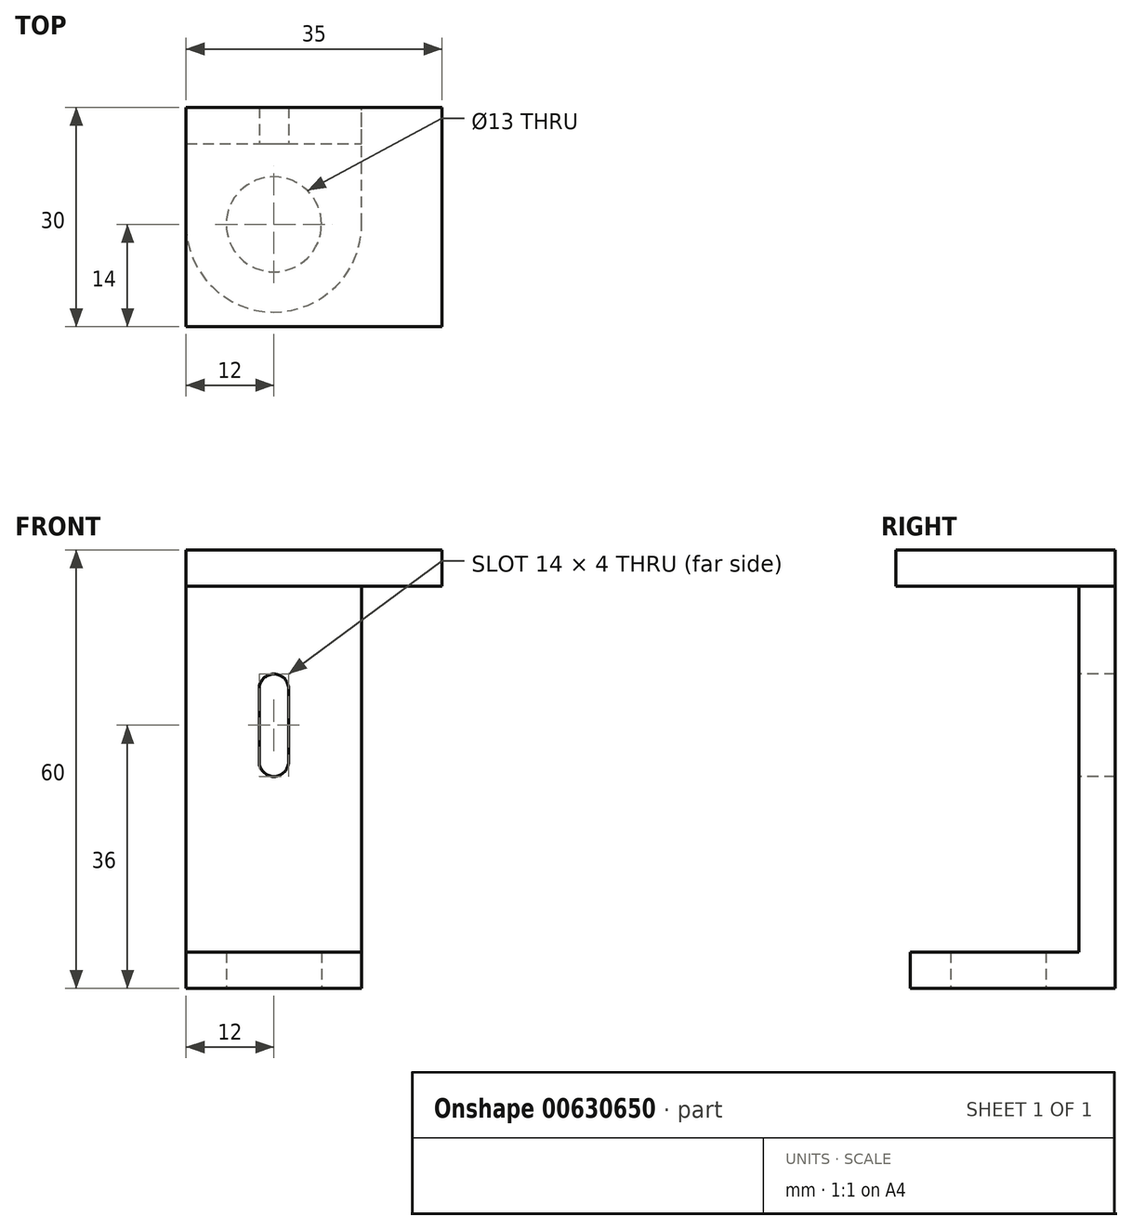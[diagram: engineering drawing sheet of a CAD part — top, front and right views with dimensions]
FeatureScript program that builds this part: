
annotation { "Feature Type Name" : "Feature", "Feature Type Description" : "" }
export const myFeature = defineFeature(function(context is Context, id is Id, definition is map)
    precondition{}
    {
        {
            var Q0;
            Q0=qCreatedBy(makeId("Top.planeOp"),FACE);
            var sketch = newSketch(context, id + "F0", { "sketchPlane" : qUnion([Q0])});
            skCircle(sketch, "E0", {"center": v(0, 0) * mm, "radius": 6.5 * mm});
            skArc(sketch, "E1", {"start": v(-12, 0) * mm, "mid": v(0, -12) * mm, "end": v(12, 0) * mm});
            skLineSegment(sketch, "E2.top", {"start": v(-12, 16) * mm, "end": v(12, 16) * mm});
            skLineSegment(sketch, "E2.left", {"start": v(-12, 0) * mm, "end": v(-12, 16) * mm});
            skLineSegment(sketch, "E2.right", {"start": v(12, 0) * mm, "end": v(12, 16) * mm});
            skSolve(sketch);
        }
        {
            var Q0;
            Q0=makeQuery(id+"F0.imprint","IMPRINT",FACE,{"disambiguationData":[TD([[makeQuery(id+"F0.imprint","IMPRINT",EDGE,{"derivedFrom":sQuery(id+"F0.wireOp",EDGE,"E0")}),-1.0]])]});
            extrude(context, id + "F1", {"entities" : qUnion([Q0]), "depth" : 5 * mm, "offsetDistance" : 25 * mm});
        }
        {
            var Q0;
            Q0=makeQuery(id+"F1.opExtrude","CAP_FACE",FACE,{"disambiguationData":[OSD([sQuery(id+"F0.wireOp",EDGE,"E0"),sQuery(id+"F0.wireOp",EDGE,"E1"),sQuery(id+"F0.wireOp",EDGE,"E2.top"),sQuery(id+"F0.wireOp",EDGE,"E2.left"),sQuery(id+"F0.wireOp",EDGE,"E2.right")])],"isStart":false});
            var sketch = newSketch(context, id + "F2", { "sketchPlane" : qUnion([Q0])});
            skLineSegment(sketch, "E3.bottom", {"start": v(-12, 16) * mm, "end": v(12, 16) * mm});
            skLineSegment(sketch, "E3.top", {"start": v(-12, 11) * mm, "end": v(12, 11) * mm});
            skLineSegment(sketch, "E3.left", {"start": v(-12, 16) * mm, "end": v(-12, 11) * mm});
            skLineSegment(sketch, "E3.right", {"start": v(12, 16) * mm, "end": v(12, 11) * mm});
            skSolve(sketch);
        }
        {
            var Q0;
            Q0=makeQuery(id+"F2.imprint","IMPRINT",FACE,{"disambiguationData":[TD([[makeQuery(id+"F2.imprint","IMPRINT",EDGE,{"derivedFrom":sQuery(id+"F2.wireOp",EDGE,"E3.bottom")}),-1.0]])]});
            extrude(context, id + "F3", {"entities" : qUnion([Q0]), "operationType" : NewBodyOperationType.ADD, "depth" : 50 * mm, "offsetDistance" : 25 * mm});
        }
        {
            var Q0;
            Q0=makeQuery(id+"F3.opExtrude","SWEPT_FACE",FACE,{"disambiguationData":[OSD([sQuery(id+"F2.wireOp",EDGE,"E3.top")])]});
            var sketch = newSketch(context, id + "F4", { "sketchPlane" : qUnion([Q0])});
            skLineSegment(sketch, "E4", {"start": v(0, 41) * mm, "end": v(0, 31) * mm});
            skArc(sketch, "E5.0.startCap", {"start": v(-2, 41) * mm, "mid": v(0, 43) * mm, "end": v(2, 41) * mm});
            skArc(sketch, "E5.0.endCap", {"start": v(2, 31) * mm, "mid": v(0, 29) * mm, "end": v(-2, 31) * mm});
            skLineSegment(sketch, "E5.0.left", {"start": v(2, 41) * mm, "end": v(2, 31) * mm});
            skLineSegment(sketch, "E5.0.right", {"start": v(-2, 41) * mm, "end": v(-2, 31) * mm});
            skSolve(sketch);
        }
        {
            var Q0;
            Q0=qSketchRegion(id+"F4",true);
            extrude(context, id + "F5", {"entities" : qUnion([Q0]), "operationType" : NewBodyOperationType.REMOVE, "endBound" : BoundingType.THROUGH_ALL, "oppositeDirection" : true, "depth" : 25 * mm, "offsetDistance" : 25 * mm});
        }
        {
            var Q0;
            Q0=makeQuery(id+"F3.opExtrude","CAP_FACE",FACE,{"disambiguationData":[OSD([sQuery(id+"F2.wireOp",EDGE,"E3.bottom"),sQuery(id+"F2.wireOp",EDGE,"E3.top"),sQuery(id+"F2.wireOp",EDGE,"E3.left"),sQuery(id+"F2.wireOp",EDGE,"E3.right")])],"isStart":false});
            var sketch = newSketch(context, id + "F6", { "sketchPlane" : qUnion([Q0])});
            skLineSegment(sketch, "E6.bottom", {"start": v(-12, 16) * mm, "end": v(23, 16) * mm});
            skLineSegment(sketch, "E6.top", {"start": v(-12, -14) * mm, "end": v(23, -14) * mm});
            skLineSegment(sketch, "E6.left", {"start": v(-12, 16) * mm, "end": v(-12, -14) * mm});
            skLineSegment(sketch, "E6.right", {"start": v(23, 16) * mm, "end": v(23, -14) * mm});
            skSolve(sketch);
        }
        {
            var Q0;
            {var subQ3=sQuery(id+"F6.wireOp",EDGE,"E6.top");Q0=makeQuery(id+"F6.imprint","IMPRINT",FACE,{"disambiguationData":[TD([[makeQuery(id+"F6.imprint","IMPRINT",EDGE,{"derivedFrom":subQ3}),1.0]])]});}
            var Q1;
            {var subQ4=makeQuery(id+"F3.opExtrude","CAP_EDGE",EDGE,{"disambiguationData":[OSD([sQuery(id+"F2.wireOp",EDGE,"E3.top")])],"isStart":false});Q1=makeQuery(id+"F6.imprint","IMPRINT",FACE,{"disambiguationData":[TD([[makeQuery(id+"F6.imprint","IMPRINT",EDGE,{"derivedFrom":subQ4}),1.0]])]});}
            extrude(context, id + "F7", {"entities" : qUnion([Q0, Q1]), "operationType" : NewBodyOperationType.ADD, "depth" : 5 * mm, "offsetDistance" : 25 * mm});
        }
    });
